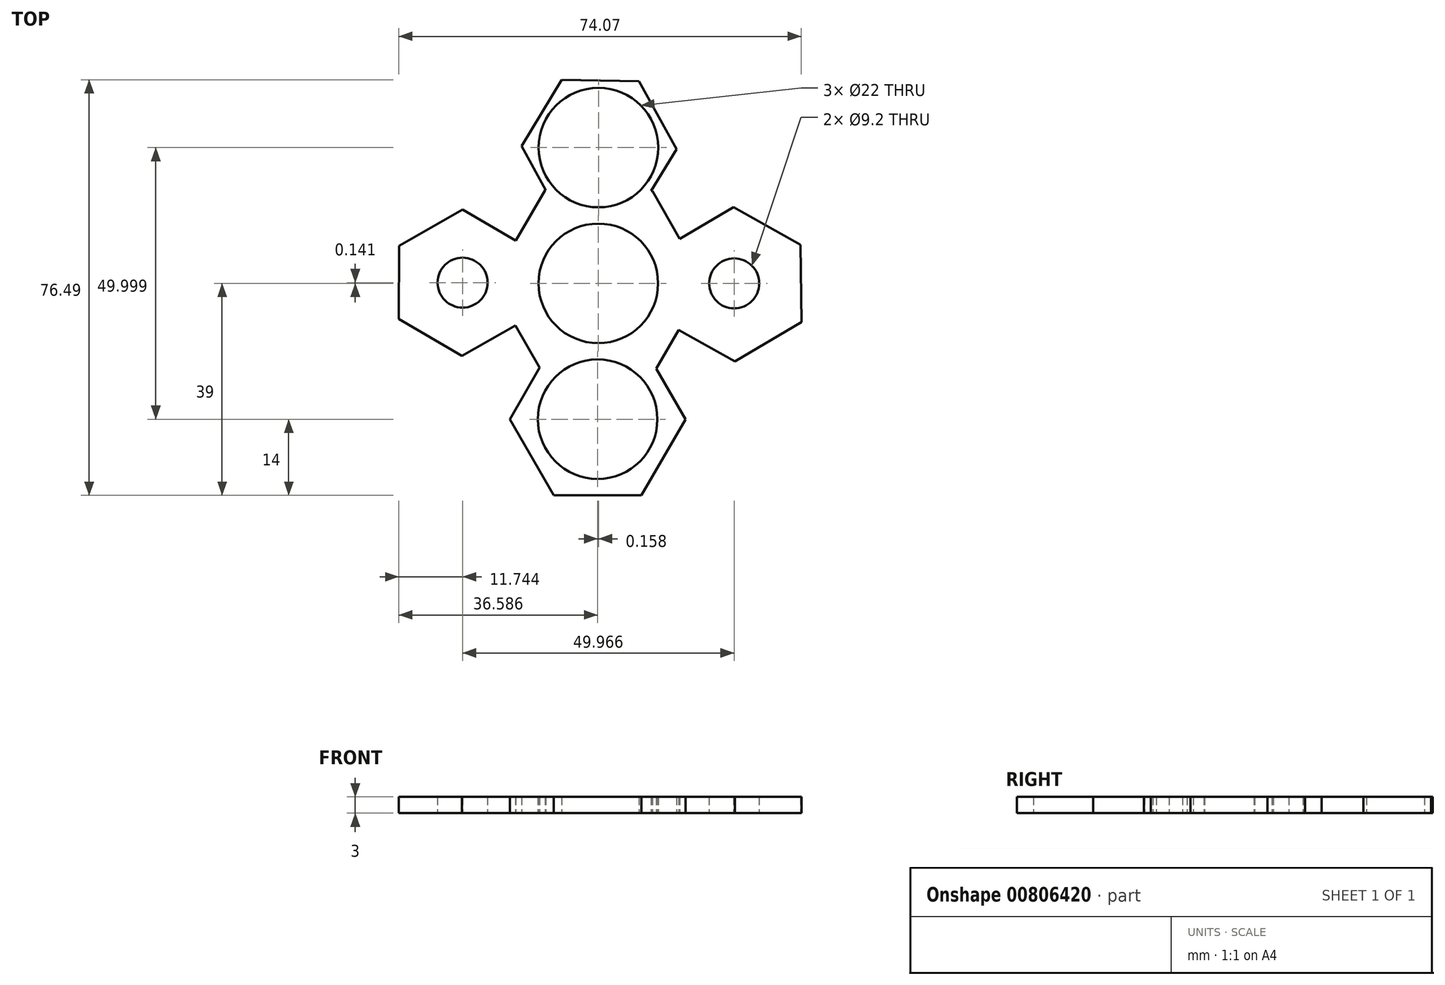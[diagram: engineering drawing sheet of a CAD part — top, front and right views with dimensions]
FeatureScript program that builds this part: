
annotation { "Feature Type Name" : "Feature", "Feature Type Description" : "" }
export const myFeature = defineFeature(function(context is Context, id is Id, definition is map)
    precondition{}
    {
        {
            var Q0;
            Q0=qCreatedBy(makeId("Top.planeOp"),FACE);
            var sketch = newSketch(context, id + "F0", { "sketchPlane" : qUnion([Q0])});
            skCircle(sketch, "E0", {"center": v(0, 0) * mm, "radius": 11 * mm});
            skLineSegment(sketch, "E1.0", {"start": v(9.94, 17.02) * mm, "end": v(14.97, 8.17) * mm});
            skLineSegment(sketch, "E1.1", {"start": v(14.8, -8.55) * mm, "end": v(10.65, -15.67) * mm});
            skLineSegment(sketch, "E1.3", {"start": v(-10.8, -15.5) * mm, "end": v(-15.23, -7.75) * mm});
            skLineSegment(sketch, "E1.4", {"start": v(-15.16, 7.9) * mm, "end": v(-9.77, 17.12) * mm});
            skLineSegment(sketch, "E1.5", {"start": v(-9.77, 17.12) * mm, "end": v(-9.63, 17.12) * mm});
            skPoint(sketch, "E1.0.midPoint", {"position": v(14.83, 8.43) * mm});
            skLineSegment(sketch, "E2.0", {"start": v(14.38, 24.7) * mm, "end": v(9.73, 17.02) * mm});
            skLineSegment(sketch, "E2.2", {"start": v(-9.63, 17.12) * mm, "end": v(-14.13, 25.3) * mm});
            skLineSegment(sketch, "E2.3", {"start": v(-14.13, 25.3) * mm, "end": v(-6.75, 37.49) * mm});
            skLineSegment(sketch, "E2.4", {"start": v(-6.75, 37.49) * mm, "end": v(7.5, 37.2) * mm});
            skLineSegment(sketch, "E2.5", {"start": v(7.5, 37.2) * mm, "end": v(14.38, 24.7) * mm});
            skPoint(sketch, "E2.0.midPoint", {"position": v(10.69, 18.6) * mm});
            skLineSegment(sketch, "E3.0", {"start": v(37.22, 7.1) * mm, "end": v(37.36, -7.1) * mm});
            skLineSegment(sketch, "E3.1", {"start": v(37.36, -7.1) * mm, "end": v(25.14, -14.38) * mm});
            skLineSegment(sketch, "E3.2", {"start": v(25.14, -14.38) * mm, "end": v(14.8, -8.55) * mm});
            skLineSegment(sketch, "E3.4", {"start": v(14.97, 8.17) * mm, "end": v(24.88, 14) * mm});
            skLineSegment(sketch, "E3.5", {"start": v(24.88, 14) * mm, "end": v(37.22, 7.1) * mm});
            skPoint(sketch, "E3.0.midPoint", {"position": v(37.3, 0) * mm});
            skArc(sketch, "E4.cCircle", {"start": v(0.01, -11) * mm, "mid": v(-0.05, -11) * mm, "end": v(-0.12, -11) * mm, "construction": true});
            skLineSegment(sketch, "E4.0", {"start": v(-0.12, -11) * mm, "end": v(0.12, -11) * mm});
            skLineSegment(sketch, "E4.1", {"start": v(10.65, -15.67) * mm, "end": v(16.04, -25) * mm});
            skLineSegment(sketch, "E4.2", {"start": v(16.04, -25) * mm, "end": v(7.96, -39) * mm});
            skLineSegment(sketch, "E4.3", {"start": v(7.96, -39) * mm, "end": v(-8.2, -39) * mm});
            skLineSegment(sketch, "E4.4", {"start": v(-8.2, -39) * mm, "end": v(-16.3, -25) * mm});
            skLineSegment(sketch, "E4.5", {"start": v(-16.3, -25) * mm, "end": v(-10.8, -15.5) * mm});
            skPoint(sketch, "E4.0.midPoint", {"position": v(-0.12, -11) * mm});
            skLineSegment(sketch, "E5.0", {"start": v(-36.7, -6.56) * mm, "end": v(-36.64, 6.92) * mm});
            skLineSegment(sketch, "E5.1", {"start": v(-36.64, 6.92) * mm, "end": v(-24.93, 13.6) * mm});
            skLineSegment(sketch, "E5.2", {"start": v(-24.93, 13.6) * mm, "end": v(-15.16, 7.9) * mm});
            skLineSegment(sketch, "E5.4", {"start": v(-15.22, -7.74) * mm, "end": v(-25.07, -13.36) * mm});
            skLineSegment(sketch, "E5.5", {"start": v(-25.07, -13.36) * mm, "end": v(-36.7, -6.56) * mm});
            skPoint(sketch, "E5.0.midPoint", {"position": v(-36.67, 0.18) * mm});
            skLineSegment(sketch, "E6.trimOffspring", {"start": v(9.73, 17.02) * mm, "end": v(9.94, 17.02) * mm});
            skPoint(sketch, "E7.orphan", {"position": v(-7.26, 12.8) * mm});
            skPoint(sketch, "E8.orphan", {"position": v(7, 12.5) * mm});
            skPoint(sketch, "E9.orphan", {"position": v(12.65, 6.8) * mm});
            skPoint(sketch, "E10.orphan", {"position": v(12.78, -7.4) * mm});
            skArc(sketch, "E11.trimOffspring", {"start": v(14.74, -8.67) * mm, "mid": v(14.77, -8.6) * mm, "end": v(14.8, -8.55) * mm, "construction": true});
            skPoint(sketch, "E12.orphan", {"position": v(7.96, -11) * mm});
            skPoint(sketch, "E13.orphan", {"position": v(-8.2, -11) * mm});
            skPoint(sketch, "E14.orphan", {"position": v(-13.36, -6.67) * mm});
            skPoint(sketch, "E15.orphan", {"position": v(19.71, -0.16) * mm});
            skCircle(sketch, "E16", {"center": v(0.03, 25) * mm, "radius": 11 * mm});
            skCircle(sketch, "E17", {"center": v(-0.12, -25) * mm, "radius": 11 * mm});
            skLineSegment(sketch, "E18", {"start": v(0, 0) * mm, "end": v(25, 0) * mm});
            skLineSegment(sketch, "E19", {"start": v(0.03, 0) * mm, "end": v(0, 0) * mm});
            skCircle(sketch, "E20", {"center": v(25, 0) * mm, "radius": 4.6 * mm});
            skCircle(sketch, "E21", {"center": v(-24.97, 0.14) * mm, "radius": 4.6 * mm});
            skSolve(sketch);
        }
        {
            var Q0;
            Q0 = qSketchRegion(id + "F0", true);
            extrude(context, id + "F1", {"entities" : qUnion([Q0]), "depth" : 3 * mm, "offsetDistance" : 25 * mm});
        }
    });
